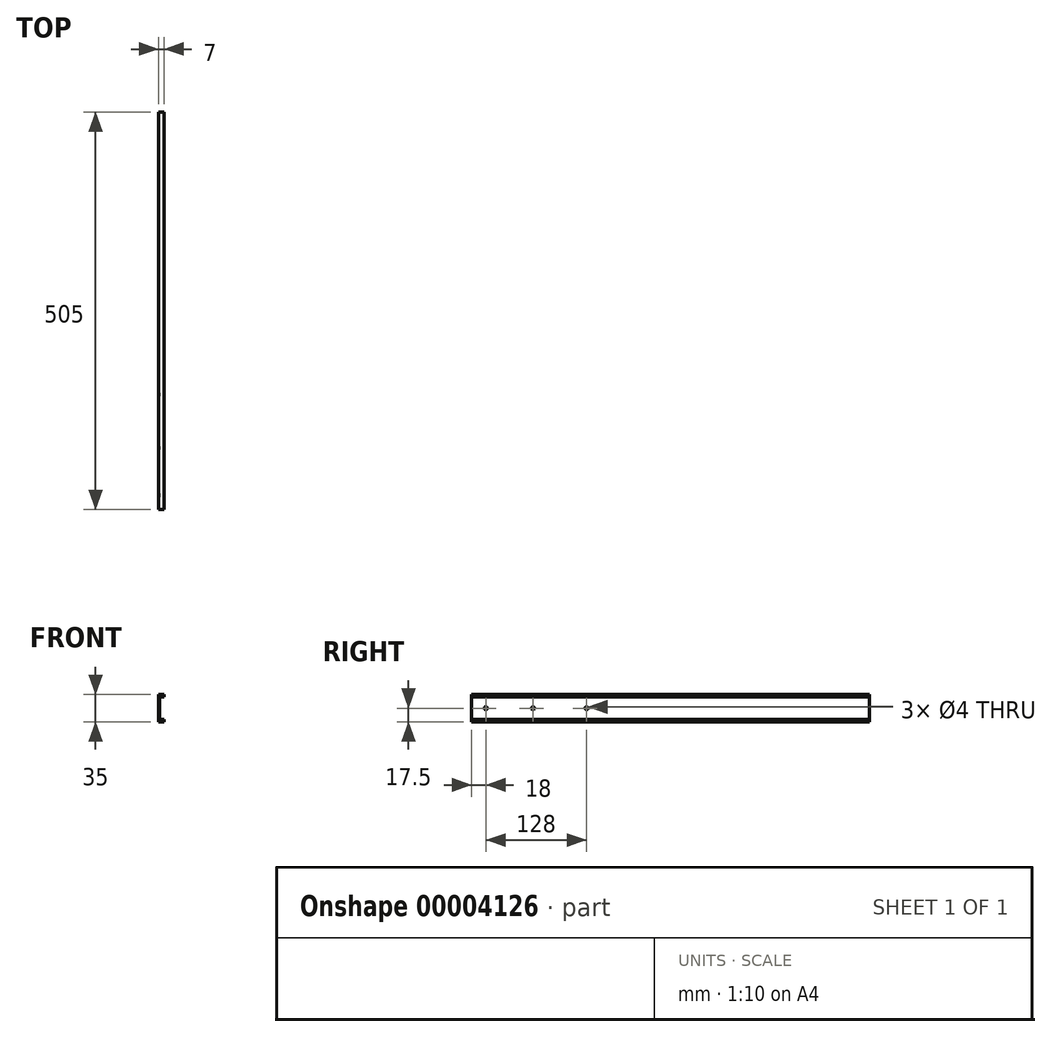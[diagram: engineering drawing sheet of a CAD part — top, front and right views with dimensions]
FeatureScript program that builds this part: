
annotation { "Feature Type Name" : "Feature", "Feature Type Description" : "" }
export const myFeature = defineFeature(function(context is Context, id is Id, definition is map)
    precondition{}
    {
        {
            var Q0;
            Q0=qCreatedBy(makeId("Front.planeOp"),FACE);
            var sketch = newSketch(context, id + "F0", { "sketchPlane" : qUnion([Q0])});
            skLineSegment(sketch, "E0", {"start": v(0, 0) * mm, "end": v(0, 17.5) * mm});
            skLineSegment(sketch, "E1", {"start": v(0, 17.5) * mm, "end": v(7, 17.5) * mm});
            skLineSegment(sketch, "E2", {"start": v(1.5, 14.25) * mm, "end": v(1.5, 0) * mm});
            skLineSegment(sketch, "E3", {"start": v(1.5, 14.25) * mm, "end": v(7, 14.25) * mm});
            skLineSegment(sketch, "E4", {"start": v(7, 14.25) * mm, "end": v(7, 17.5) * mm});
            skLineSegment(sketch, "E5.0.MirrorCS", {"start": v(1.5, -14.25) * mm, "end": v(7, -14.25) * mm});
            skLineSegment(sketch, "E5.1.MirrorCS", {"start": v(7, -14.25) * mm, "end": v(7, -17.5) * mm});
            skLineSegment(sketch, "E5.2.MirrorCS", {"start": v(0, -17.5) * mm, "end": v(7, -17.5) * mm});
            skLineSegment(sketch, "E6.0.MirrorCS", {"start": v(0, 0) * mm, "end": v(0, -17.5) * mm});
            skLineSegment(sketch, "E6.1.MirrorCS", {"start": v(1.5, -14.25) * mm, "end": v(1.5, 0) * mm});
            skSolve(sketch);
        }
        {
            var Q0;
            Q0 = qSketchRegion(id + "F0", true);
            extrude(context, id + "F1", {"entities" : qUnion([Q0]), "depth" : 505 * mm});
        }
        {
            var Q0;
            Q0=makeQuery(id+"F1.opExtrude","SWEPT_FACE",FACE,{"disambiguationData":[OSD([sQuery(id+"F0.wireOp",EDGE,"E6.1.MirrorCS")])]});
            var sketch = newSketch(context, id + "F2", { "sketchPlane" : qUnion([Q0])});
            skLineSegment(sketch, "E7", {"start": v(-505, 0) * mm, "end": v(-469, 0) * mm});
            skCircle(sketch, "E8", {"center": v(-427, 0) * mm, "radius": 2 * mm});
            skCircle(sketch, "E9", {"center": v(-359, 0) * mm, "radius": 2 * mm});
            skCircle(sketch, "E10", {"center": v(-487, 0) * mm, "radius": 2 * mm});
            skSolve(sketch);
        }
        {
            var Q0;
            Q0=makeQuery(id+"F2.imprint","IMPRINT",FACE,{"disambiguationData":[TD([[makeQuery(id+"F2.imprint","IMPRINT",EDGE,{"derivedFrom":sQuery(id+"F2.wireOp",EDGE,"E8")}),1.0]])]});
            var Q1;
            Q1=makeQuery(id+"F2.imprint","IMPRINT",FACE,{"disambiguationData":[TD([[makeQuery(id+"F2.imprint","IMPRINT",EDGE,{"derivedFrom":sQuery(id+"F2.wireOp",EDGE,"E9")}),1.0]])]});
            var Q2;
            {var subQ0=sQuery(id+"F2.wireOp",EDGE,"E10");var subQ1=sQuery(id+"F2.wireOp",EDGE,"E7");var subQ3=makeQuery(id+"F2.imprint","INTERSECT",VERTEX,{"disambiguationData":[OD(0.0)],"derivedFrom":[subQ1,subQ0]});Q2=makeQuery(id+"F2.imprint","IMPRINT",FACE,{"disambiguationData":[TD([[makeQuery(id+"F2.imprint","IMPRINT",EDGE,{"disambiguationData":[TD([[subQ3,-1.0]])],"derivedFrom":subQ1}),-1.0]])]});}
            var Q3;
            {var subQ0=sQuery(id+"F2.wireOp",EDGE,"E10");var subQ1=sQuery(id+"F2.wireOp",EDGE,"E7");var subQ3=makeQuery(id+"F2.imprint","INTERSECT",VERTEX,{"disambiguationData":[OD(0.0)],"derivedFrom":[subQ1,subQ0]});Q3=makeQuery(id+"F2.imprint","IMPRINT",FACE,{"disambiguationData":[TD([[makeQuery(id+"F2.imprint","IMPRINT",EDGE,{"disambiguationData":[TD([[subQ3,-1.0]])],"derivedFrom":subQ1}),1.0]])]});}
            extrude(context, id + "F3", {"entities" : qUnion([Q0, Q1, Q2, Q3]), "operationType" : NewBodyOperationType.REMOVE, "oppositeDirection" : true, "depth" : 25 * mm});
        }
    });
